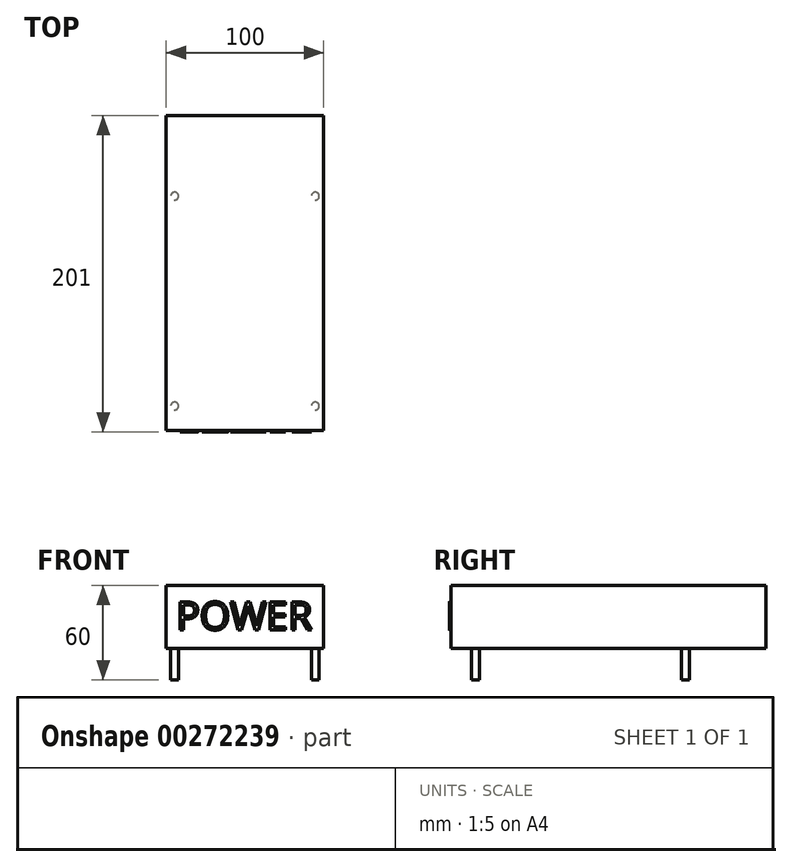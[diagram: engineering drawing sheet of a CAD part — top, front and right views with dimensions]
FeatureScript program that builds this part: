
annotation { "Feature Type Name" : "Feature", "Feature Type Description" : "" }
export const myFeature = defineFeature(function(context is Context, id is Id, definition is map)
    precondition{}
    {
        {
            var Q0;
            Q0=qCreatedBy(makeId("Top.planeOp"),FACE);
            var sketch = newSketch(context, id + "F0", { "sketchPlane" : qUnion([Q0])});
            skLineSegment(sketch, "E0.bottom", {"start": v(50, -82.15) * mm, "end": v(-50, -82.15) * mm});
            skLineSegment(sketch, "E0.top", {"start": v(50, 117.85) * mm, "end": v(-50, 117.85) * mm});
            skLineSegment(sketch, "E0.left", {"start": v(50, -82.15) * mm, "end": v(50, 117.85) * mm});
            skLineSegment(sketch, "E0.right", {"start": v(-50, -82.15) * mm, "end": v(-50, 117.85) * mm});
            skPoint(sketch, "E0.middle", {"position": v(0, 17.85) * mm});
            skSolve(sketch);
        }
        {
            var Q0;
            Q0=makeQuery(id+"F0.imprint","IMPRINT",FACE,{"disambiguationData":[TD([[makeQuery(id+"F0.imprint","IMPRINT",EDGE,{"derivedFrom":sQuery(id+"F0.wireOp",EDGE,"E0.bottom")}),-1.0]])]});
            extrude(context, id + "F1", {"entities" : qUnion([Q0]), "depth" : 40 * mm});
        }
        {
            var Q0;
            Q0=makeQuery(id+"F1.opExtrude","SWEPT_FACE",FACE,{"disambiguationData":[OSD([sQuery(id+"F0.wireOp",EDGE,"E0.bottom")])]});
            var sketch = newSketch(context, id + "F2", { "sketchPlane" : qUnion([Q0])});
            skText(sketch, "E1", { "text": "POWER", "fontName": "OpenSans-Regular.ttf"});
            const initialGuessF2  = {"E1": [-0.04361, 0.01182, 1, 0, 0.01785]};
            skSetInitialGuess(sketch, initialGuessF2);
            skSolve(sketch);
        }
        {
            var Q0;
            Q0 = qSketchRegion(id + "F2", true);
            extrude(context, id + "F3", {"entities" : qUnion([Q0]), "operationType" : NewBodyOperationType.ADD, "depth" : 1 * mm});
        }
        {
            var Q0;
            Q0=makeQuery(id+"F1.opExtrude","CAP_FACE",FACE,{"disambiguationData":[OSD([sQuery(id+"F0.wireOp",EDGE,"E0.bottom"),sQuery(id+"F0.wireOp",EDGE,"E0.top"),sQuery(id+"F0.wireOp",EDGE,"E0.left"),sQuery(id+"F0.wireOp",EDGE,"E0.right")])],"isStart":true});
            var sketch = newSketch(context, id + "F4", { "sketchPlane" : qUnion([Q0])});
            skCircle(sketch, "E2", {"center": v(-44.7, 66.65) * mm, "radius": 2.5 * mm});
            skCircle(sketch, "E3.MirrorC", {"center": v(44.7, 66.65) * mm, "radius": 2.5 * mm});
            skCircle(sketch, "E4.MirrorC", {"center": v(44.7, -66.65) * mm, "radius": 2.5 * mm});
            skCircle(sketch, "E5.MirrorC", {"center": v(-44.7, -66.65) * mm, "radius": 2.5 * mm});
            skSolve(sketch);
        }
        {
            var Q0;
            Q0 = qSketchRegion(id + "F4", true);
            extrude(context, id + "F5", {"entities" : qUnion([Q0]), "operationType" : NewBodyOperationType.ADD, "depth" : 20 * mm});
        }
    });
